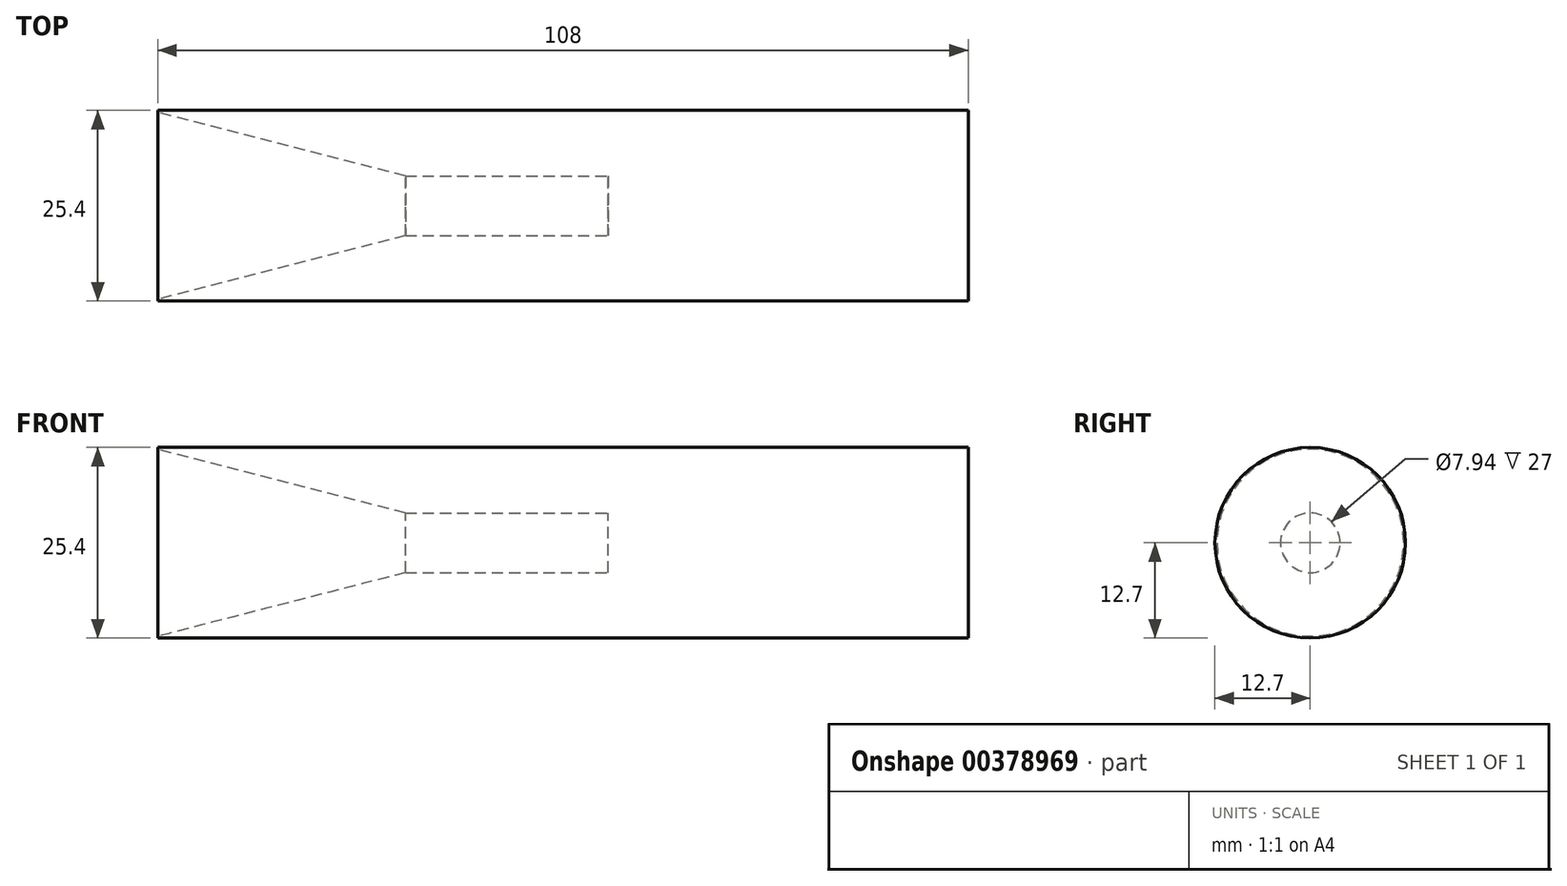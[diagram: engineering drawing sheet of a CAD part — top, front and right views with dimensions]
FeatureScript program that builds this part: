
annotation { "Feature Type Name" : "Feature", "Feature Type Description" : "" }
export const myFeature = defineFeature(function(context is Context, id is Id, definition is map)
    precondition{}
    {
        {
            var Q0;
            Q0=qCreatedBy(makeId("Front.planeOp"),FACE);
            var sketch = newSketch(context, id + "F0", { "sketchPlane" : qUnion([Q0])});
            skLineSegment(sketch, "E0", {"start": v(0, 0) * mm, "end": v(6, 0) * mm});
            skLineSegment(sketch, "E1", {"start": v(6, 0) * mm, "end": v(6, 3.97) * mm});
            skLineSegment(sketch, "E2", {"start": v(6, 3.97) * mm, "end": v(-21, 3.97) * mm});
            skLineSegment(sketch, "E3", {"start": v(-21, 3.97) * mm, "end": v(-54, 12.45) * mm});
            skLineSegment(sketch, "E4", {"start": v(-54, 12.45) * mm, "end": v(-54, 0) * mm});
            skLineSegment(sketch, "E5", {"start": v(-54, 0) * mm, "end": v(0, 0) * mm});
            skSolve(sketch);
        }
        {
            var Q0;
            Q0=qCreatedBy(makeId("Right.planeOp"),FACE);
            var sketch = newSketch(context, id + "F1", { "sketchPlane" : qUnion([Q0])});
            skCircle(sketch, "E6", {"center": v(0, 0) * mm, "radius": 12.7 * mm});
            skSolve(sketch);
        }
        {
            var Q0;
            Q0=makeQuery(id+"F1.imprint","IMPRINT",FACE,{"disambiguationData":[TD([[makeQuery(id+"F1.imprint","IMPRINT",EDGE,{"derivedFrom":sQuery(id+"F1.wireOp",EDGE,"E6")}),1.0]])]});
            extrude(context, id + "F2", {"entities" : qUnion([Q0]), "endBound" : BoundingType.SYMMETRIC, "depth" : 108 * mm});
        }
        {
            var Q0;
            Q0 = qSketchRegion(id + "F0", true);
            var Q1;
            Q1=sQuery(id+"F0.wireOp",EDGE,"E5");
            revolve(context, id + "F3", {"operationType" : NewBodyOperationType.REMOVE, "entities" : qUnion([Q0]), "axis" : qUnion([Q1]), "revolveType" : RevolveType.FULL, "oppositeDirection" : true});
        }
    });
